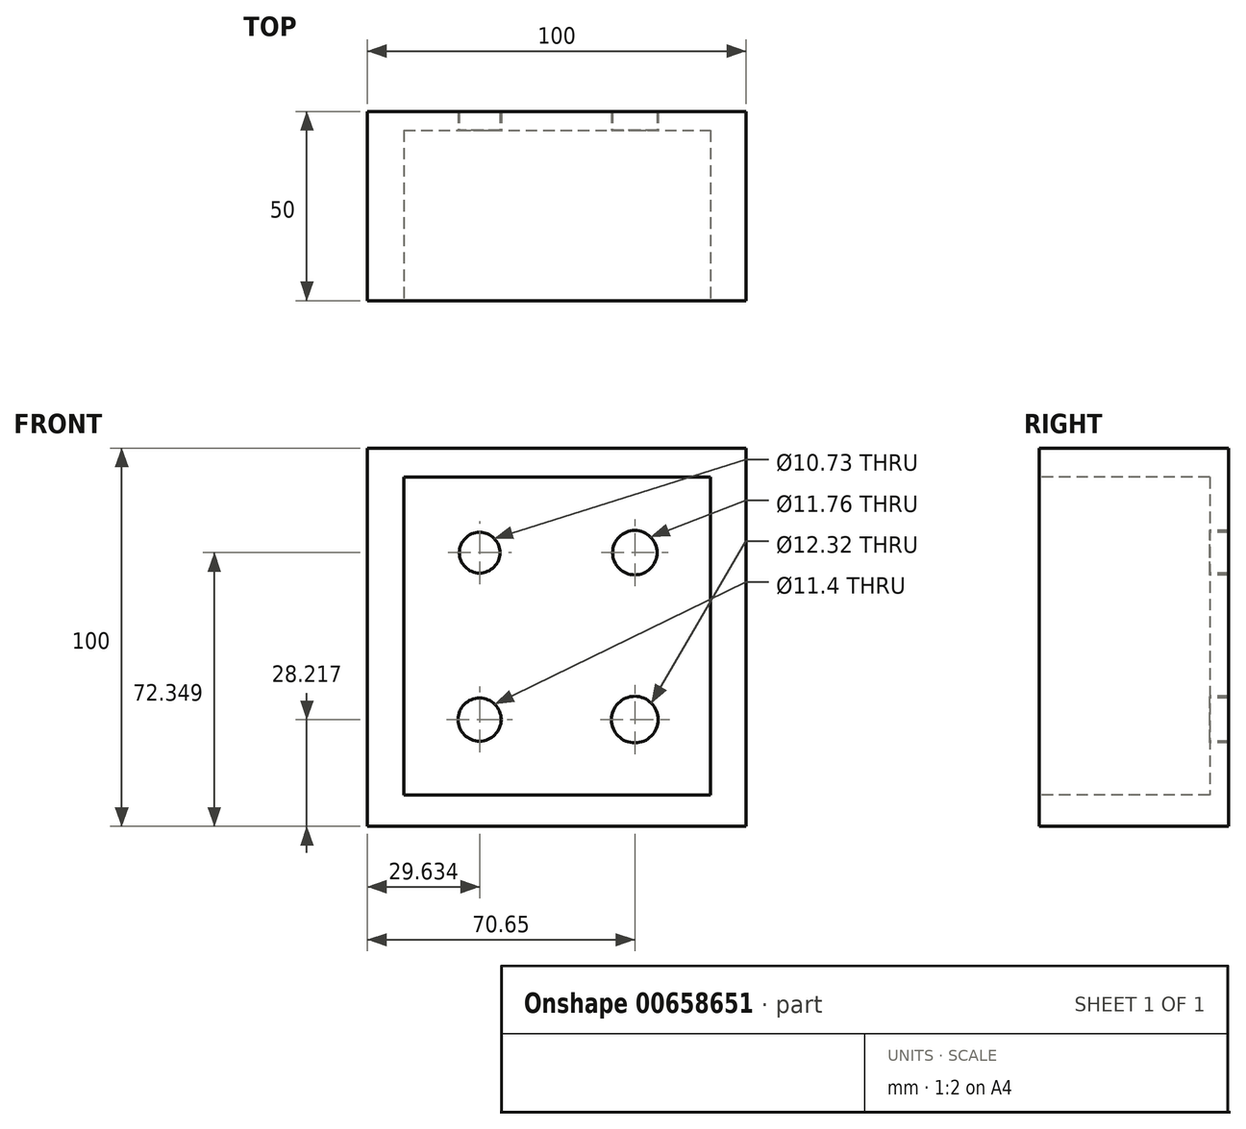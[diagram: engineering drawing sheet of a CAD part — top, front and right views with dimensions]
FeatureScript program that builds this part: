
annotation { "Feature Type Name" : "Feature", "Feature Type Description" : "" }
export const myFeature = defineFeature(function(context is Context, id is Id, definition is map)
    precondition{}
    {
        {
            var Q0;
            Q0=qCreatedBy(makeId("Front.planeOp"),FACE);
            var sketch = newSketch(context, id + "F0", { "sketchPlane" : qUnion([Q0])});
            skLineSegment(sketch, "E0.bottom", {"start": v(-50, 50) * mm, "end": v(50, 50) * mm});
            skLineSegment(sketch, "E0.top", {"start": v(-50, -50) * mm, "end": v(50, -50) * mm});
            skLineSegment(sketch, "E0.left", {"start": v(-50, 50) * mm, "end": v(-50, -50) * mm});
            skLineSegment(sketch, "E0.right", {"start": v(50, 50) * mm, "end": v(50, -50) * mm});
            skSolve(sketch);
        }
        {
            var Q0;
            Q0=makeQuery(id+"F0.imprint","IMPRINT",FACE,{"disambiguationData":[TD([[makeQuery(id+"F0.imprint","IMPRINT",EDGE,{"derivedFrom":sQuery(id+"F0.wireOp",EDGE,"E0.bottom")}),-1.0]])]});
            extrude(context, id + "F1", {"entities" : qUnion([Q0]), "depth" : 50 * mm, "offsetDistance" : 25 * mm});
        }
        {
            var Q0;
            Q0=makeQuery(id+"F1.opExtrude","CAP_FACE",FACE,{"disambiguationData":[OSD([sQuery(id+"F0.wireOp",EDGE,"E0.bottom"),sQuery(id+"F0.wireOp",EDGE,"E0.top"),sQuery(id+"F0.wireOp",EDGE,"E0.left"),sQuery(id+"F0.wireOp",EDGE,"E0.right")])],"isStart":false});
            var sketch = newSketch(context, id + "F2", { "sketchPlane" : qUnion([Q0])});
            skLineSegment(sketch, "E1.bottom", {"start": v(-40.37, 42.35) * mm, "end": v(40.65, 42.35) * mm});
            skLineSegment(sketch, "E1.top", {"start": v(-40.37, -41.78) * mm, "end": v(40.65, -41.78) * mm});
            skLineSegment(sketch, "E1.left", {"start": v(-40.37, 42.35) * mm, "end": v(-40.37, -41.78) * mm});
            skLineSegment(sketch, "E1.right", {"start": v(40.65, 42.35) * mm, "end": v(40.65, -41.78) * mm});
            skSolve(sketch);
        }
        {
            var Q0;
            Q0 = qSketchRegion(id + "F2", true);
            extrude(context, id + "F3", {"entities" : qUnion([Q0]), "operationType" : NewBodyOperationType.REMOVE, "oppositeDirection" : true, "depth" : 45 * mm, "offsetDistance" : 25 * mm});
        }
        {
            var Q0;
            Q0=makeQuery(id+"F3.boolean.opBoolean","COPY",FACE,{"derivedFrom":makeQuery(id+"F3.opExtrude","CAP_FACE",FACE,{"disambiguationData":[OSD([sQuery(id+"F2.wireOp",EDGE,"E1.bottom"),sQuery(id+"F2.wireOp",EDGE,"E1.top"),sQuery(id+"F2.wireOp",EDGE,"E1.left"),sQuery(id+"F2.wireOp",EDGE,"E1.right")])],"isStart":false})});
            var sketch = newSketch(context, id + "F4", { "sketchPlane" : qUnion([Q0])});
            skCircle(sketch, "E2", {"center": v(-20.37, 22.35) * mm, "radius": 5.37 * mm});
            skCircle(sketch, "E3", {"center": v(20.65, 22.35) * mm, "radius": 5.88 * mm});
            skCircle(sketch, "E4", {"center": v(-20.37, -21.78) * mm, "radius": 5.7 * mm});
            skCircle(sketch, "E5", {"center": v(20.65, -21.78) * mm, "radius": 6.16 * mm});
            skSolve(sketch);
        }
        {
            var Q0;
            Q0=makeQuery(id+"F4.imprint","IMPRINT",FACE,{"disambiguationData":[TD([[makeQuery(id+"F4.imprint","IMPRINT",EDGE,{"derivedFrom":sQuery(id+"F4.wireOp",EDGE,"E2")}),-1.0]])]});
            var sketch = newSketch(context, id + "F5", { "sketchPlane" : qUnion([Q0])});
            skSolve(sketch);
        }
        {
            var Q0;
            Q0=makeQuery(id+"F5.imprint","IMPRINT",FACE,{"disambiguationData":[TD([[makeQuery(id+"F5.imprint","IMPRINT",EDGE,{"derivedFrom":makeQuery(id+"F4.imprint","IMPRINT",EDGE,{"derivedFrom":sQuery(id+"F4.wireOp",EDGE,"E2")})}),1.0]])]});
            var Q1;
            Q1=makeQuery(id+"F5.imprint","IMPRINT",FACE,{"disambiguationData":[TD([[makeQuery(id+"F5.imprint","IMPRINT",EDGE,{"derivedFrom":makeQuery(id+"F4.imprint","IMPRINT",EDGE,{"derivedFrom":sQuery(id+"F4.wireOp",EDGE,"E3")})}),1.0]])]});
            var Q2;
            Q2=makeQuery(id+"F5.imprint","IMPRINT",FACE,{"disambiguationData":[TD([[makeQuery(id+"F5.imprint","IMPRINT",EDGE,{"derivedFrom":makeQuery(id+"F4.imprint","IMPRINT",EDGE,{"derivedFrom":sQuery(id+"F4.wireOp",EDGE,"E5")})}),1.0]])]});
            var Q3;
            Q3=makeQuery(id+"F5.imprint","IMPRINT",FACE,{"disambiguationData":[TD([[makeQuery(id+"F5.imprint","IMPRINT",EDGE,{"derivedFrom":makeQuery(id+"F4.imprint","IMPRINT",EDGE,{"derivedFrom":sQuery(id+"F4.wireOp",EDGE,"E4")})}),1.0]])]});
            extrude(context, id + "F6", {"entities" : qUnion([Q0, Q1, Q2, Q3]), "operationType" : NewBodyOperationType.REMOVE, "oppositeDirection" : true, "depth" : 25 * mm, "offsetDistance" : 25 * mm});
        }
        {
            var Q0;
            Q0=makeQuery(id+"F4.imprint","IMPRINT",FACE,{"disambiguationData":[TD([[makeQuery(id+"F4.imprint","IMPRINT",EDGE,{"derivedFrom":sQuery(id+"F4.wireOp",EDGE,"E4")}),1.0]])]});
            var Q1;
            Q1=makeQuery(id+"F4.imprint","IMPRINT",FACE,{"disambiguationData":[TD([[makeQuery(id+"F4.imprint","IMPRINT",EDGE,{"derivedFrom":sQuery(id+"F4.wireOp",EDGE,"E2")}),1.0]])]});
            var Q2;
            Q2=makeQuery(id+"F4.imprint","IMPRINT",FACE,{"disambiguationData":[TD([[makeQuery(id+"F4.imprint","IMPRINT",EDGE,{"derivedFrom":sQuery(id+"F4.wireOp",EDGE,"E3")}),1.0]])]});
            var Q3;
            Q3=makeQuery(id+"F4.imprint","IMPRINT",FACE,{"disambiguationData":[TD([[makeQuery(id+"F4.imprint","IMPRINT",EDGE,{"derivedFrom":sQuery(id+"F4.wireOp",EDGE,"E5")}),1.0]])]});
            extrude(context, id + "F7", {"entities" : qUnion([Q0, Q1, Q2, Q3]), "operationType" : NewBodyOperationType.REMOVE, "oppositeDirection" : true, "depth" : 19.5 * mm, "offsetDistance" : 25 * mm});
        }
    });
